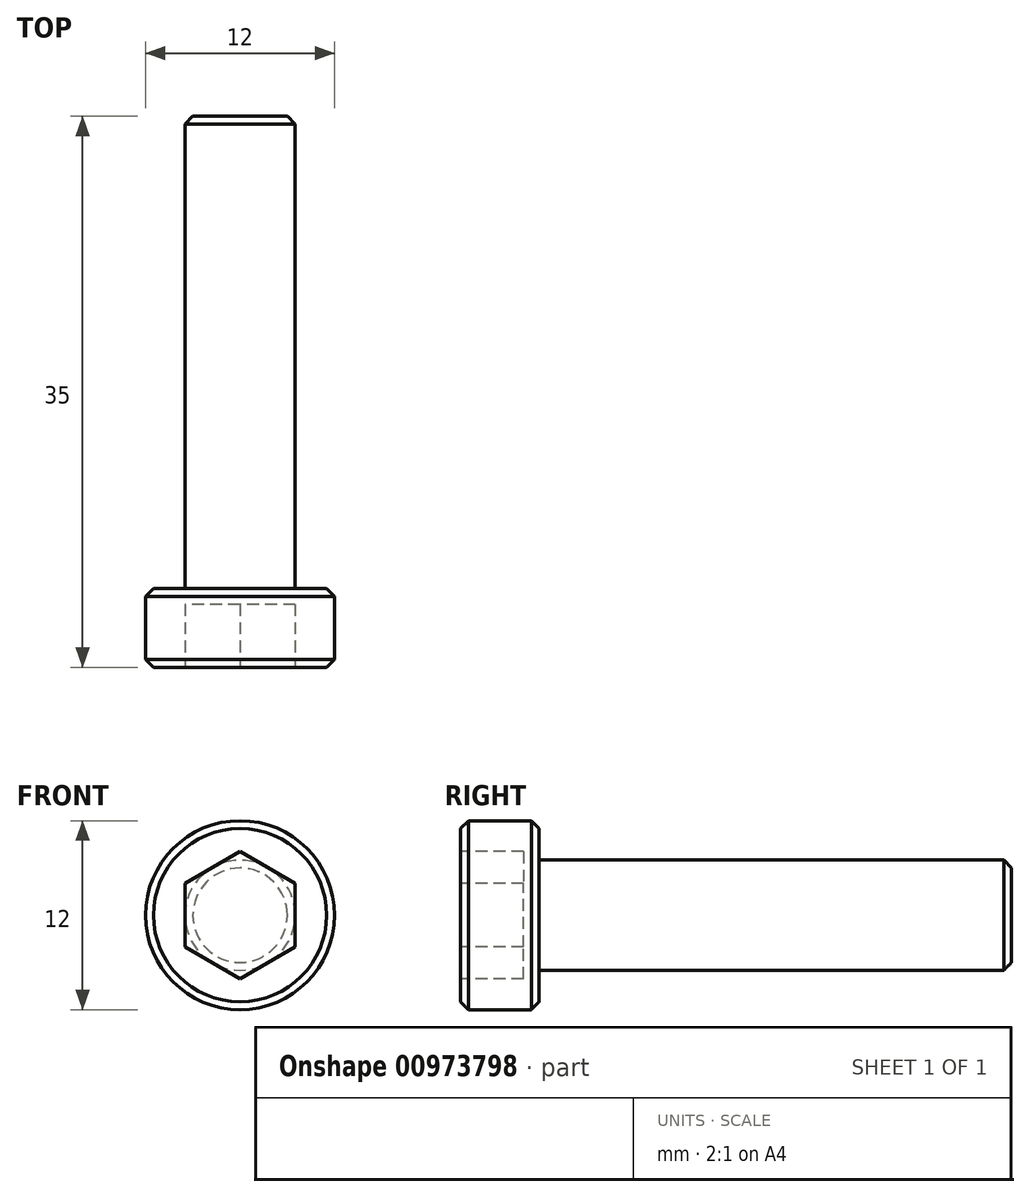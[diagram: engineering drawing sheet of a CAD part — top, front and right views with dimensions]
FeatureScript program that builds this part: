
annotation { "Feature Type Name" : "Feature", "Feature Type Description" : "" }
export const myFeature = defineFeature(function(context is Context, id is Id, definition is map)
    precondition{}
    {
        {
            var Q0;
            Q0=qCreatedBy(makeId("Front.planeOp"),FACE);
            var sketch = newSketch(context, id + "F0", { "sketchPlane" : qUnion([Q0])});
            skCircle(sketch, "E0", {"center": v(0, 0) * mm, "radius": 3.5 * mm});
            skSolve(sketch);
        }
        {
            var Q0;
            Q0 = qSketchRegion(id + "F0", true);
            extrude(context, id + "F1", {"entities" : qUnion([Q0]), "oppositeDirection" : true, "depth" : 30 * mm, "offsetDistance" : 25 * mm});
        }
        {
            var Q0;
            Q0=makeQuery(id+"F1.opExtrude","CAP_FACE",FACE,{"disambiguationData":[OSD([sQuery(id+"F0.wireOp",EDGE,"E0")])],"isStart":true});
            var sketch = newSketch(context, id + "F2", { "sketchPlane" : qUnion([Q0])});
            skCircle(sketch, "E1", {"center": v(0, 0) * mm, "radius": 6 * mm});
            skSolve(sketch);
        }
        {
            var Q0;
            Q0 = qSketchRegion(id + "F2", true);
            extrude(context, id + "F3", {"entities" : qUnion([Q0]), "operationType" : NewBodyOperationType.ADD, "depth" : 5 * mm, "offsetDistance" : 25 * mm});
        }
        {
            var Q0;
            Q0=makeQuery(id+"F3.opExtrude","CAP_EDGE",EDGE,{"disambiguationData":[OSD([sQuery(id+"F2.wireOp",EDGE,"E1")])],"isStart":false});
            var Q1;
            Q1=makeQuery(id+"F3.opExtrude","CAP_EDGE",EDGE,{"disambiguationData":[OSD([sQuery(id+"F2.wireOp",EDGE,"E1")])],"isStart":true});
            var Q2;
            Q2=makeQuery(id+"F1.opExtrude","CAP_EDGE",EDGE,{"disambiguationData":[OSD([sQuery(id+"F0.wireOp",EDGE,"E0")])],"isStart":false});
            var Q3;
            Q3=makeQuery(id+"F1.opExtrude","CAP_EDGE",EDGE,{"disambiguationData":[OSD([sQuery(id+"F0.wireOp",EDGE,"E0")])],"isStart":true});
            chamfer(context, id + "F4", {"entities" : qUnion([Q0, Q1, Q2, Q3]), "width" : 0.5 * mm, "tangentPropagation" : true});
        }
        {
            var Q0;
            Q0=makeQuery(id+"F3.opExtrude","CAP_FACE",FACE,{"disambiguationData":[OSD([sQuery(id+"F2.wireOp",EDGE,"E1")])],"isStart":false});
            var sketch = newSketch(context, id + "F5", { "sketchPlane" : qUnion([Q0])});
            skCircle(sketch, "E2.cCircle", {"center": v(0, 0) * mm, "radius": 3.5 * mm, "construction": true});
            skLineSegment(sketch, "E2.0", {"start": v(-3.5, -2.02) * mm, "end": v(-3.5, 2.02) * mm});
            skLineSegment(sketch, "E2.1", {"start": v(-3.5, 2.02) * mm, "end": v(0, 4.04) * mm});
            skLineSegment(sketch, "E2.2", {"start": v(0, 4.04) * mm, "end": v(3.5, 2.02) * mm});
            skLineSegment(sketch, "E2.3", {"start": v(3.5, 2.02) * mm, "end": v(3.5, -2.02) * mm});
            skLineSegment(sketch, "E2.4", {"start": v(3.5, -2.02) * mm, "end": v(0, -4.04) * mm});
            skLineSegment(sketch, "E2.5", {"start": v(0, -4.04) * mm, "end": v(-3.5, -2.02) * mm});
            skPoint(sketch, "E2.0.midPoint", {"position": v(-3.5, 0) * mm});
            skLineSegment(sketch, "E3", {"start": v(0, 0.1) * mm, "end": v(0, 4.04) * mm, "construction": true});
            skSolve(sketch);
        }
        {
            var Q0;
            Q0 = qSketchRegion(id + "F5", true);
            extrude(context, id + "F6", {"entities" : qUnion([Q0]), "operationType" : NewBodyOperationType.REMOVE, "oppositeDirection" : true, "depth" : 4 * mm, "offsetDistance" : 25 * mm});
        }
    });
